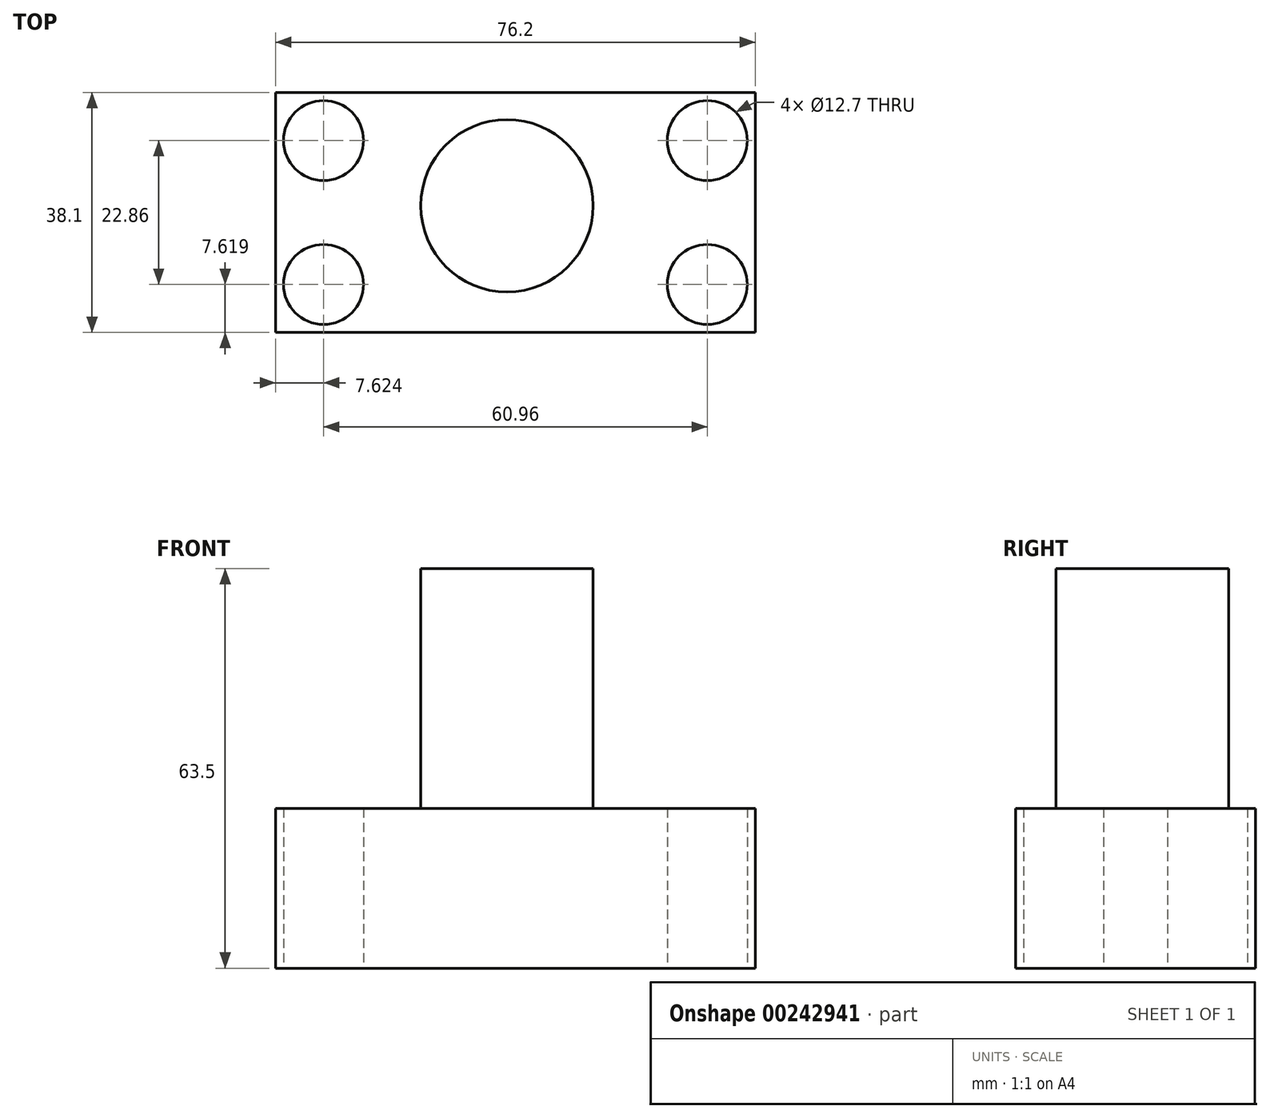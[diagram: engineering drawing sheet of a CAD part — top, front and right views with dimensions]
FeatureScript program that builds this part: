
annotation { "Feature Type Name" : "Feature", "Feature Type Description" : "" }
export const myFeature = defineFeature(function(context is Context, id is Id, definition is map)
    precondition{}
    {
        {
            var Q0;
            Q0=qCreatedBy(makeId("Top.planeOp"),FACE);
            var sketch = newSketch(context, id + "F0", { "sketchPlane" : qUnion([Q0])});
            skLineSegment(sketch, "E0.bottom", {"start": v(-46.64, 7.35) * mm, "end": v(29.56, 7.35) * mm});
            skLineSegment(sketch, "E0.top", {"start": v(-46.64, -30.75) * mm, "end": v(29.56, -30.75) * mm});
            skLineSegment(sketch, "E0.left", {"start": v(-46.64, 7.35) * mm, "end": v(-46.64, -30.75) * mm});
            skLineSegment(sketch, "E0.right", {"start": v(29.56, 7.35) * mm, "end": v(29.56, -30.75) * mm});
            skSolve(sketch);
        }
        {
            var Q0;
            Q0 = qSketchRegion(id + "F0", true);
            extrude(context, id + "F1", {"entities" : qUnion([Q0]), "depth" : 25.4 * mm});
        }
        {
            var Q0;
            Q0=qCreatedBy(makeId("Top.planeOp"),FACE);
            var sketch = newSketch(context, id + "F2", { "sketchPlane" : qUnion([Q0])});
            skCircle(sketch, "E1", {"center": v(-39.02, -0.27) * mm, "radius": 6.35 * mm});
            skSolve(sketch);
        }
        {
            var Q0;
            Q0 = qSketchRegion(id + "F2", true);
            extrude(context, id + "F3", {"entities" : qUnion([Q0]), "operationType" : NewBodyOperationType.REMOVE, "depth" : 25.4 * mm});
        }
        {
            var Q0;
            Q0=qCreatedBy(makeId("Top.planeOp"),FACE);
            var sketch = newSketch(context, id + "F4", { "sketchPlane" : qUnion([Q0])});
            skCircle(sketch, "E2", {"center": v(21.94, -0.27) * mm, "radius": 6.35 * mm});
            skSolve(sketch);
        }
        {
            var Q0;
            Q0 = qSketchRegion(id + "F4", true);
            extrude(context, id + "F5", {"entities" : qUnion([Q0]), "operationType" : NewBodyOperationType.REMOVE, "depth" : 25.4 * mm});
        }
        {
            var Q0;
            Q0=qCreatedBy(makeId("Top.planeOp"),FACE);
            var sketch = newSketch(context, id + "F6", { "sketchPlane" : qUnion([Q0])});
            skCircle(sketch, "E3", {"center": v(-39.02, -23.13) * mm, "radius": 6.35 * mm});
            skSolve(sketch);
        }
        {
            var Q0;
            Q0 = qSketchRegion(id + "F6", true);
            extrude(context, id + "F7", {"entities" : qUnion([Q0]), "operationType" : NewBodyOperationType.REMOVE, "depth" : 25.4 * mm});
        }
        {
            var Q0;
            Q0=qCreatedBy(makeId("Top.planeOp"),FACE);
            var sketch = newSketch(context, id + "F8", { "sketchPlane" : qUnion([Q0])});
            skCircle(sketch, "E4", {"center": v(21.94, -23.13) * mm, "radius": 6.35 * mm});
            skSolve(sketch);
        }
        {
            var Q0;
            Q0 = qSketchRegion(id + "F8", true);
            extrude(context, id + "F9", {"entities" : qUnion([Q0]), "operationType" : NewBodyOperationType.REMOVE, "depth" : 25.4 * mm});
        }
        {
            var Q0;
            Q0=makeQuery(id+"F1.opExtrude","CAP_FACE",FACE,{"disambiguationData":[OSD([sQuery(id+"F0.wireOp",EDGE,"E0.bottom"),sQuery(id+"F0.wireOp",EDGE,"E0.top"),sQuery(id+"F0.wireOp",EDGE,"E0.left"),sQuery(id+"F0.wireOp",EDGE,"E0.right")])],"isStart":false});
            var sketch = newSketch(context, id + "F10", { "sketchPlane" : qUnion([Q0])});
            skCircle(sketch, "E5", {"center": v(-9.88, -10.64) * mm, "radius": 13.7 * mm});
            skSolve(sketch);
        }
        {
            var Q0;
            Q0 = qSketchRegion(id + "F10", true);
            extrude(context, id + "F11", {"entities" : qUnion([Q0]), "operationType" : NewBodyOperationType.ADD, "depth" : 38.1 * mm});
        }
        {
            var Q0;
            Q0=qCreatedBy(makeId("Front.planeOp"),FACE);
            var sketch = newSketch(context, id + "F12", { "sketchPlane" : qUnion([Q0])});
            skLineSegment(sketch, "E6.bottom", {"start": v(-31.42, 45.77) * mm, "end": v(-18.72, 45.77) * mm});
            skLineSegment(sketch, "E6.top", {"start": v(-31.42, 33.07) * mm, "end": v(-18.72, 33.07) * mm});
            skLineSegment(sketch, "E6.left", {"start": v(-31.42, 45.77) * mm, "end": v(-31.42, 33.07) * mm});
            skLineSegment(sketch, "E6.right", {"start": v(-18.72, 45.77) * mm, "end": v(-18.72, 33.07) * mm});
            skSolve(sketch);
        }
        {
            var Q0;
            Q0=makeQuery(id+"F12.imprint","IMPRINT",FACE,{"disambiguationData":[TD([[makeQuery(id+"F12.imprint","IMPRINT",EDGE,{"derivedFrom":sQuery(id+"F12.wireOp",EDGE,"E6.bottom")}),-1.0]])]});
            var Q1;
            Q1=makeQuery(id+"F11.opExtrude","CAP_EDGE",EDGE,{"disambiguationData":[OSD([sQuery(id+"F10.wireOp",EDGE,"E5")])],"isStart":false});
            revolve(context, id + "F13", {"operationType" : NewBodyOperationType.REMOVE, "entities" : qUnion([Q0]), "axis" : qUnion([Q1]), "revolveType" : RevolveType.FULL, "oppositeDirection" : true});
        }
    });
